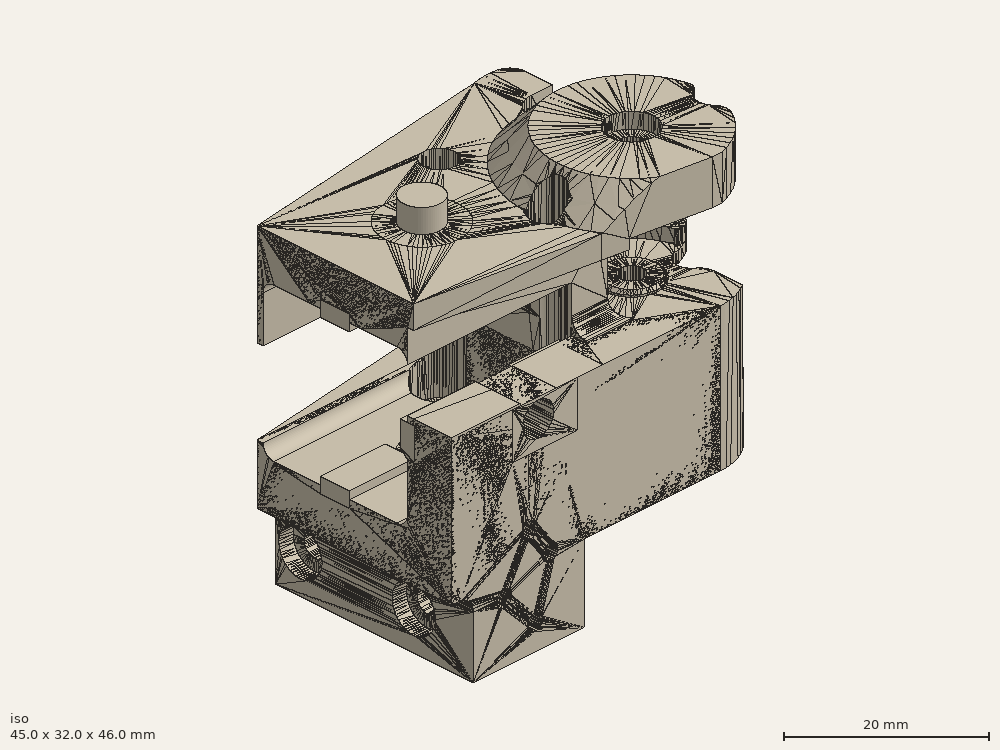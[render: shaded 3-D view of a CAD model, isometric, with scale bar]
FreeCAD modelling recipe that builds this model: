
FCSTD DOCUMENT  (FreeCAD 0.18R16146 (Git))
Label: carrier-right
License: All rights reserved
LicenseURL: http://en.wikipedia.org/wiki/All_rights_reserved
objects: Part::Box×9, Part::Cylinder×6, Part::Cut×5, Part::MultiFuse×4, Part::Feature×3, Part::Chamfer×2
note: 29 computed .brp shape members not serialized (recipe doc carries the construction recipe); baked Part::Feature solids carry a one-line shape summary decoded from their .brp

FEATURE [Part::Feature] Part__Feature  label="Y_CarriageHT_RIGHT_Body_(1)"
  Placement = pos=(-424,-201,-461.78) rot=(1,0,0;1.5708rad)
  shape: bbox 48.82 x 34.51 x 45.95 mm, 188 faces (baked)
FEATURE [Part::Box] Box  label="Cube"
  AttacherType = Attacher::AttachEngine3D
  Height = 20
  Length = 25
  Placement = pos=(-23.16,6.39,16.2) rot=(0,0,1;0rad)
  Width = 20
FEATURE [Part::Feature] Part__Feature001  label="Y_CarriageHT_RIGHT_Body_(1)001"
  Placement = pos=(-424,-201,-461.78) rot=(1,0,0;1.5708rad)
  shape: bbox 48.82 x 34.51 x 45.95 mm, 188 faces (baked)
FEATURE [Part::Cut] Cut
  Base = -> Part__Feature001
  Tool = -> Box
FEATURE [Part::Cylinder] Cylinder  label="pref"
  Angle = 360
  AttacherType = Attacher::AttachEngine3D
  Height = 10
  Placement = pos=(-8.92,16.39,35) rot=(0,0,1;0rad)
  Radius = 2.5
FEATURE [Part::Cylinder] Cylinder001  label="pref001"
  Angle = 360
  AttacherType = Attacher::AttachEngine3D
  Height = 14.2
  Placement = pos=(-8.92,16.39,2) rot=(0,0,1;0rad)
  Radius = 2.15
FEATURE [Part::Cylinder] Cylinder002  label="pref002"
  Angle = 360
  AttacherType = Attacher::AttachEngine3D
  Height = 14.2
  Placement = pos=(-8.92,16.39,2) rot=(0,0,1;0rad)
  Radius = 2.6
FEATURE [Part::Cut] Cut001
  Base = -> Cylinder002
  Tool = -> Cylinder001
FEATURE [Part::Cylinder] Cylinder003  label="pref003"
  Angle = 360
  AttacherType = Attacher::AttachEngine3D
  Height = 5.75
  Placement = pos=(-8.92,16.39,36.2) rot=(0,0,1;0rad)
  Radius = 2.15
FEATURE [Part::Cylinder] Cylinder004  label="pref004"
  Angle = 360
  AttacherType = Attacher::AttachEngine3D
  Height = 5.75
  Placement = pos=(-8.92,16.39,36.2) rot=(0,0,1;0rad)
  Radius = 2.6
FEATURE [Part::Cut] Cut002
  Base = -> Cylinder004
  Tool = -> Cylinder003
FEATURE [Part::Cylinder] Cylinder006  label="pref006"
  Angle = 360
  AttacherType = Attacher::AttachEngine3D
  Height = 6.13
  Placement = pos=(-8.92,6.38,26.2) rot=(1,0,0;1.5708rad)
  Radius = 2.15
FEATURE [Part::Box] Box001  label="Cube001"
  AttacherType = Attacher::AttachEngine3D
  Height = 3
  Length = 23
  Placement = pos=(-23,0.25,28.7) rot=(0,0,1;0rad)
  Width = 8.13
FEATURE [Part::Box] Box002  label="Cube002"
  AttacherType = Attacher::AttachEngine3D
  Height = 6
  Length = 9
  Placement = pos=(-12.5,0.25,22.7) rot=(0,0,1;0rad)
  Width = 6.13
FEATURE [Part::Cut] Cut003
  Base = -> Cut
  Tool = -> Box001
FEATURE [Part::Cut] Cut004
  Base = -> Box002
  Tool = -> Cylinder006
FEATURE [Part::Box] Box003  label="Cube003"
  AttacherType = Attacher::AttachEngine3D
  Height = 2
  Length = 9
  Placement = pos=(-20.93,14.39,15.2) rot=(0,0,1;0rad)
  Width = 4
FEATURE [Part::Box] Box004  label="Cube004"
  AttacherType = Attacher::AttachEngine3D
  Height = 2
  Length = 9
  Placement = pos=(-5.93,14.39,15.2) rot=(0,0,1;0rad)
  Width = 4
FEATURE [Part::Box] Box005  label="Cube005"
  AttacherType = Attacher::AttachEngine3D
  Height = 2
  Length = 9
  Placement = pos=(-5.93,14.39,35.2) rot=(0,0,1;0rad)
  Width = 4
FEATURE [Part::Box] Box006  label="Cube006"
  AttacherType = Attacher::AttachEngine3D
  Height = 2
  Length = 9
  Placement = pos=(-20.93,14.39,35.2) rot=(0,0,1;0rad)
  Width = 4
FEATURE [Part::Box] Box007  label="Cube007"
  AttacherType = Attacher::AttachEngine3D
  Height = 4.2
  Length = 9
  Placement = pos=(-20.93,5.39,24) rot=(0,0,1;0rad)
  Width = 2
FEATURE [Part::Box] Box008  label="Cube008"
  AttacherType = Attacher::AttachEngine3D
  Height = 4.2
  Length = 7
  Placement = pos=(-5.93,5.39,24) rot=(0,0,1;0rad)
  Width = 2
FEATURE [Part::Chamfer] Chamfer
  Base = -> Box008
  Edges = 1 edges r=1: [Edge11]
FEATURE [Part::Chamfer] Chamfer001
  Base = -> Box007
  Edges = 1 edges r=1: [Edge11]
FEATURE [Part::MultiFuse] Fusion
  Shapes = -> [Chamfer001,Chamfer,Box006,Box005,Box004,Box003]
FEATURE [Part::MultiFuse] Fusion001
  Shapes = -> [Cut004,Cut002,Cut001]
FEATURE [Part::MultiFuse] Fusion002
  Shapes = -> [Fusion,Cut003]
FEATURE [Part::MultiFuse] Fusion003  label="rev-1"
  Shapes = -> [Fusion002,Fusion001]
FEATURE [Part::Feature] Fusion003001_solid  label="rev-1-exp"
  shape: bbox 48.82 x 34.51 x 45.95 mm, 242 faces (baked)
